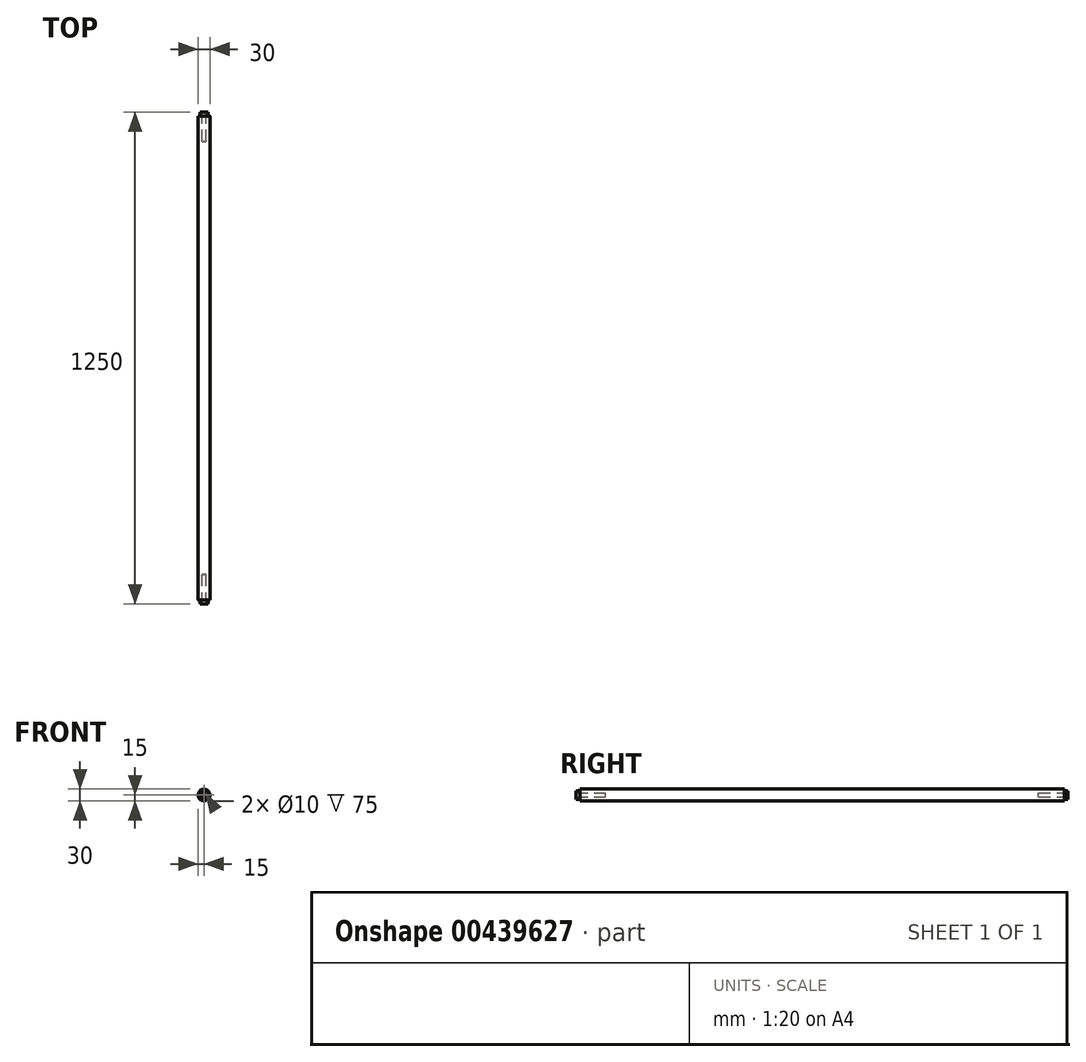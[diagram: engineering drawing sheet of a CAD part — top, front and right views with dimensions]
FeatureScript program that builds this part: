
annotation { "Feature Type Name" : "Feature", "Feature Type Description" : "" }
export const myFeature = defineFeature(function(context is Context, id is Id, definition is map)
    precondition{}
    {
        {
            var Q0;
            Q0=qCreatedBy(makeId("Front.planeOp"),FACE);
            var sketch = newSketch(context, id + "F0", { "sketchPlane" : qUnion([Q0])});
            skCircle(sketch, "E0", {"center": v(0, 0) * mm, "radius": 15 * mm});
            skCircle(sketch, "E1", {"center": v(0, 0) * mm, "radius": 5 * mm});
            skCircle(sketch, "E2.cCircle", {"center": v(0, 0) * mm, "radius": 15 * mm, "construction": true});
            skLineSegment(sketch, "E2.0", {"start": v(-10.6, 10.6) * mm, "end": v(10.6, 10.6) * mm});
            skLineSegment(sketch, "E2.1", {"start": v(10.6, 10.6) * mm, "end": v(10.6, -10.6) * mm});
            skLineSegment(sketch, "E2.2", {"start": v(10.6, -10.6) * mm, "end": v(-10.6, -10.6) * mm});
            skLineSegment(sketch, "E2.3", {"start": v(-10.6, -10.6) * mm, "end": v(-10.6, 10.6) * mm});
            skSolve(sketch);
        }
        {
            var Q0;
            Q0=makeQuery(id+"F0.imprint","IMPRINT",FACE,{"disambiguationData":[TD([[makeQuery(id+"F0.imprint","IMPRINT",EDGE,{"derivedFrom":sQuery(id+"F0.wireOp",EDGE,"E1")}),-1.0]])]});
            var Q1;
            Q1=sQuery(id+"F0.wireOp",EDGE,"E0");
            extrude(context, id + "F1", {"entities" : qUnion([Q0]), "surfaceEntities" : qUnion([Q1]), "endBound" : BoundingType.SYMMETRIC, "depth" : 1250 * mm});
        }
        {
            var Q0;
            {var subQ0=sQuery(id+"F0.wireOp",EDGE,"E2.0");Q0=makeQuery(id+"F0.imprint","IMPRINT",FACE,{"disambiguationData":[TD([[makeQuery(id+"F0.imprint","IMPRINT",EDGE,{"derivedFrom":subQ0}),1.0]])]});}
            var Q1;
            {var subQ0=sQuery(id+"F0.wireOp",EDGE,"E2.1");Q1=makeQuery(id+"F0.imprint","IMPRINT",FACE,{"disambiguationData":[TD([[makeQuery(id+"F0.imprint","IMPRINT",EDGE,{"derivedFrom":subQ0}),1.0]])]});}
            var Q2;
            {var subQ0=sQuery(id+"F0.wireOp",EDGE,"E2.2");Q2=makeQuery(id+"F0.imprint","IMPRINT",FACE,{"disambiguationData":[TD([[makeQuery(id+"F0.imprint","IMPRINT",EDGE,{"derivedFrom":subQ0}),1.0]])]});}
            var Q3;
            {var subQ0=sQuery(id+"F0.wireOp",EDGE,"E2.3");Q3=makeQuery(id+"F0.imprint","IMPRINT",FACE,{"disambiguationData":[TD([[makeQuery(id+"F0.imprint","IMPRINT",EDGE,{"derivedFrom":subQ0}),1.0]])]});}
            extrude(context, id + "F2", {"entities" : qUnion([Q0, Q1, Q2, Q3]), "operationType" : NewBodyOperationType.ADD, "endBound" : BoundingType.SYMMETRIC, "depth" : 1230 * mm});
        }
        {
            var Q0;
            Q0=makeQuery(id+"F0.imprint","IMPRINT",FACE,{"disambiguationData":[TD([[makeQuery(id+"F0.imprint","IMPRINT",EDGE,{"derivedFrom":sQuery(id+"F0.wireOp",EDGE,"E1")}),1.0]])]});
            extrude(context, id + "F3", {"entities" : qUnion([Q0]), "operationType" : NewBodyOperationType.ADD, "endBound" : BoundingType.SYMMETRIC, "depth" : 1100 * mm});
        }
    });
